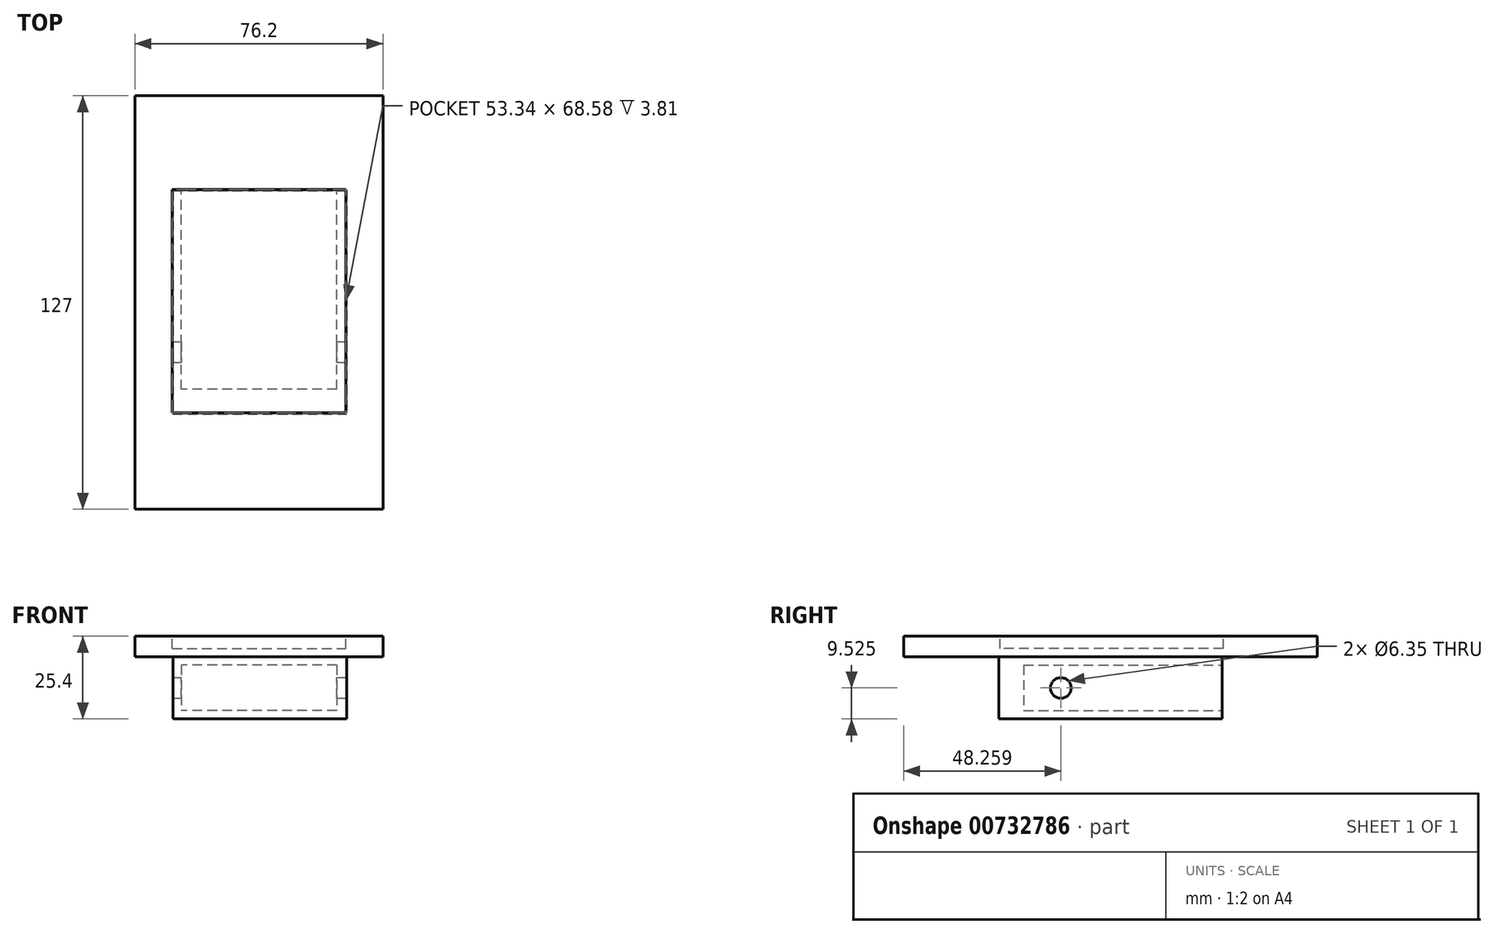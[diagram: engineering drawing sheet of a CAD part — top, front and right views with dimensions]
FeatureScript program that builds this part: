
annotation { "Feature Type Name" : "Feature", "Feature Type Description" : "" }
export const myFeature = defineFeature(function(context is Context, id is Id, definition is map)
    precondition{}
    {
        {
            var Q0;
            Q0=qCreatedBy(makeId("Top.planeOp"),FACE);
            var sketch = newSketch(context, id + "F0", { "sketchPlane" : qUnion([Q0])});
            skLineSegment(sketch, "E0.bottom", {"start": v(-26.47, 33.9) * mm, "end": v(26.87, 33.9) * mm});
            skLineSegment(sketch, "E0.top", {"start": v(-26.47, -34.68) * mm, "end": v(26.87, -34.68) * mm});
            skLineSegment(sketch, "E0.left", {"start": v(-26.47, 33.9) * mm, "end": v(-26.47, -34.68) * mm});
            skLineSegment(sketch, "E0.right", {"start": v(26.87, 33.9) * mm, "end": v(26.87, -34.68) * mm});
            skLineSegment(sketch, "E1.bottom", {"start": v(38.07, 63.1) * mm, "end": v(-38.13, 63.1) * mm});
            skLineSegment(sketch, "E1.top", {"start": v(38.07, -63.9) * mm, "end": v(-38.13, -63.9) * mm});
            skLineSegment(sketch, "E1.left", {"start": v(38.07, 63.1) * mm, "end": v(38.07, -63.9) * mm});
            skLineSegment(sketch, "E1.right", {"start": v(-38.13, 63.1) * mm, "end": v(-38.13, -63.9) * mm});
            skLineSegment(sketch, "E2", {"start": v(-37.68, -0.4) * mm, "end": v(-26.47, -0.4) * mm});
            skLineSegment(sketch, "E3", {"start": v(26.87, -0.4) * mm, "end": v(38.07, -0.4) * mm});
            skLineSegment(sketch, "E4", {"start": v(-0.03, 33.9) * mm, "end": v(-0.03, 63.1) * mm});
            skLineSegment(sketch, "E5", {"start": v(16.32, -63.9) * mm, "end": v(16.32, -34.68) * mm});
            skLineSegment(sketch, "E6", {"start": v(-0.03, 63.1) * mm, "end": v(-0.03, 37.7) * mm});
            skLineSegment(sketch, "E7", {"start": v(-0.03, 37.7) * mm, "end": v(12.67, 37.7) * mm});
            skLineSegment(sketch, "E8.MirrorCS", {"start": v(-0.03, 37.7) * mm, "end": v(-12.73, 37.7) * mm});
            skSolve(sketch);
        }
        {
            var Q0;
            {var subQ4=sQuery(id+"F0.wireOp",EDGE,"E0.left");var subQ10=makeQuery(id+"F0.imprint","IMPRINT",VERTEX,{"derivedFrom":subQ4});Q0=makeQuery(id+"F0.imprint","IMPRINT",FACE,{"disambiguationData":[TD([[makeQuery(id+"F0.imprint","IMPRINT",EDGE,{"disambiguationData":[TD([[subQ10,1.0]])],"derivedFrom":subQ4}),1.0]])]});}
            extrude(context, id + "F1", {"entities" : qUnion([Q0]), "oppositeDirection" : true, "depth" : 19.05 * mm, "offsetDistance" : 25.4 * mm});
        }
        {
            var Q0;
            Q0=makeQuery(id+"F1.opExtrude","SWEPT_FACE",FACE,{"disambiguationData":[OSD([sQuery(id+"F0.wireOp",EDGE,"E0.bottom")])]});
            var sketch = newSketch(context, id + "F2", { "sketchPlane" : qUnion([Q0])});
            skLineSegment(sketch, "E9", {"start": v(26.47, 0) * mm, "end": v(26.47, -19.05) * mm});
            skLineSegment(sketch, "E10", {"start": v(26.47, -19.05) * mm, "end": v(-26.87, -19.05) * mm});
            skLineSegment(sketch, "E11", {"start": v(-26.87, -19.05) * mm, "end": v(-26.87, 0) * mm});
            skLineSegment(sketch, "E12", {"start": v(-26.87, 0) * mm, "end": v(26.47, 0) * mm});
            skLineSegment(sketch, "E13", {"start": v(26.47, 0) * mm, "end": v(23.93, 0) * mm});
            skLineSegment(sketch, "E14", {"start": v(23.93, 0) * mm, "end": v(23.93, -2.54) * mm});
            skLineSegment(sketch, "E15.MirrorCS", {"start": v(-23.93, 0) * mm, "end": v(-23.93, -2.54) * mm});
            skLineSegment(sketch, "E16", {"start": v(-23.93, -2.54) * mm, "end": v(23.93, -2.54) * mm});
            skLineSegment(sketch, "E17", {"start": v(26.47, -19.05) * mm, "end": v(23.93, -19.05) * mm});
            skLineSegment(sketch, "E18", {"start": v(23.93, -19.05) * mm, "end": v(23.93, -16.51) * mm});
            skLineSegment(sketch, "E19.MirrorCS", {"start": v(-23.93, -19.05) * mm, "end": v(-23.93, -16.51) * mm});
            skLineSegment(sketch, "E20", {"start": v(-23.93, -2.54) * mm, "end": v(-23.93, -16.51) * mm});
            skLineSegment(sketch, "E21", {"start": v(-23.93, -16.51) * mm, "end": v(23.93, -16.51) * mm});
            skLineSegment(sketch, "E22", {"start": v(23.93, -2.54) * mm, "end": v(23.93, -16.51) * mm});
            skSolve(sketch);
        }
        {
            var Q0;
            Q0=makeQuery(id+"F2.imprint","IMPRINT",FACE,{"disambiguationData":[TD([[makeQuery(id+"F2.imprint","IMPRINT",EDGE,{"derivedFrom":sQuery(id+"F2.wireOp",EDGE,"E16")}),-1.0]])]});
            extrude(context, id + "F3", {"entities" : qUnion([Q0]), "operationType" : NewBodyOperationType.REMOVE, "oppositeDirection" : true, "depth" : 60.96 * mm, "offsetDistance" : 25.4 * mm});
        }
        {
            var Q0;
            Q0=makeQuery(id+"F0.imprint","IMPRINT",FACE,{"disambiguationData":[TD([[makeQuery(id+"F0.imprint","IMPRINT",EDGE,{"derivedFrom":sQuery(id+"F0.wireOp",EDGE,"gSL48M3m-er1I-eWqx-o3Fm-BarbDNzvo99A.bottom")}),1.0]])]});
            var Q1;
            {var subQ7=sQuery(id+"F0.wireOp",EDGE,"E3");Q1=makeQuery(id+"F0.imprint","IMPRINT",FACE,{"disambiguationData":[TD([[makeQuery(id+"F0.imprint","IMPRINT",EDGE,{"derivedFrom":subQ7}),-1.0]])]});}
            var Q2;
            {var subQ0=sQuery(id+"F0.wireOp",EDGE,"E4");Q2=makeQuery(id+"F0.imprint","IMPRINT",FACE,{"disambiguationData":[TD([[makeQuery(id+"F0.imprint","IMPRINT",EDGE,{"derivedFrom":subQ0}),1.0]])]});}
            var Q3;
            {var subQ0=sQuery(id+"F0.wireOp",EDGE,"b93ae854-abed-4926-95a7-5670e14655770.MirrorCS");Q3=makeQuery(id+"F0.imprint","IMPRINT",FACE,{"disambiguationData":[TD([[makeQuery(id+"F0.imprint","IMPRINT",EDGE,{"derivedFrom":subQ0}),-1.0]])]});}
            var Q4;
            {var subQ3=sQuery(id+"F0.wireOp",EDGE,"E3");Q4=makeQuery(id+"F0.imprint","IMPRINT",FACE,{"disambiguationData":[TD([[makeQuery(id+"F0.imprint","IMPRINT",EDGE,{"derivedFrom":subQ3}),1.0]])]});}
            var Q5;
            {var subQ4=sQuery(id+"F0.wireOp",EDGE,"E0.left");var subQ10=makeQuery(id+"F0.imprint","IMPRINT",VERTEX,{"derivedFrom":subQ4});Q5=makeQuery(id+"F0.imprint","IMPRINT",FACE,{"disambiguationData":[TD([[makeQuery(id+"F0.imprint","IMPRINT",EDGE,{"disambiguationData":[TD([[subQ10,1.0]])],"derivedFrom":subQ4}),1.0]])]});}
            extrude(context, id + "F4", {"entities" : qUnion([Q0, Q1, Q2, Q3, Q4, Q5]), "operationType" : NewBodyOperationType.ADD, "depth" : 6.35 * mm, "offsetDistance" : 25.4 * mm});
        }
        {
            var Q0;
            Q0=makeQuery(id+"F1.opExtrude","SWEPT_FACE",FACE,{"disambiguationData":[OSD([sQuery(id+"F0.wireOp",EDGE,"E0.right")])]});
            var sketch = newSketch(context, id + "F5", { "sketchPlane" : qUnion([Q0])});
            skLineSegment(sketch, "E23", {"start": v(33.9, -19.05) * mm, "end": v(-34.68, -19.05) * mm});
            skLineSegment(sketch, "E24", {"start": v(-34.68, -19.05) * mm, "end": v(-34.68, 0) * mm});
            skLineSegment(sketch, "E25", {"start": v(-34.68, 0) * mm, "end": v(33.9, 0) * mm});
            skLineSegment(sketch, "E26", {"start": v(33.9, 0) * mm, "end": v(33.9, -19.05) * mm});
            skPoint(sketch, "E27", {"position": v(-15.63, -9.52) * mm});
            skPoint(sketch, "E27.positionSnap0", {"position": v(-34.68, -9.52) * mm});
            skSolve(sketch);
        }
        {
            var Q0;
            Q0=sQuery(id+"F5.wireOp",VERTEX,"E27");
            var Q1;
            Q1=makeQuery(id+"F1.opExtrude","SWEPT_BODY",BODY,{"disambiguationData":[OSD([sQuery(id+"F0.wireOp",EDGE,"E0.bottom"),sQuery(id+"F0.wireOp",EDGE,"E0.top"),sQuery(id+"F0.wireOp",EDGE,"E0.left"),sQuery(id+"F0.wireOp",EDGE,"E0.right")])]});
            hole(context, id + "F6", {"style" : HoleStyle.SIMPLE, "endStyle" : HoleEndStyle.THROUGH, "holeDiameter" : 6.35 * mm, "majorDiameter" : 6.35 * mm, "isTappedThrough" : true, "tappedDepth" : 12.7 * mm, "tapClearance" : 3, "locations" : qUnion([Q0]), "scope" : qUnion([Q1])});
        }
        {
            var Q0;
            Q0=makeQuery(id+"F4.opExtrude","CAP_FACE",FACE,{"disambiguationData":[OSD([sQuery(id+"F0.wireOp",EDGE,"E1.bottom"),sQuery(id+"F0.wireOp",EDGE,"E1.top"),sQuery(id+"F0.wireOp",EDGE,"E1.left"),sQuery(id+"F0.wireOp",EDGE,"E1.right")])],"isStart":false});
            var sketch = newSketch(context, id + "F7", { "sketchPlane" : qUnion([Q0])});
            skLineSegment(sketch, "E28", {"start": v(0, 0) * mm, "end": v(26.67, 0) * mm});
            skLineSegment(sketch, "E29", {"start": v(26.67, 0) * mm, "end": v(26.67, 34.3) * mm});
            skLineSegment(sketch, "E30.MirrorCS", {"start": v(-26.67, 0) * mm, "end": v(-26.67, 34.3) * mm});
            skLineSegment(sketch, "E31.MirrorCS", {"start": v(26.67, 0) * mm, "end": v(26.67, -34.3) * mm});
            skLineSegment(sketch, "E32.MirrorCS", {"start": v(-26.67, 0) * mm, "end": v(-26.67, -34.3) * mm});
            skLineSegment(sketch, "E33", {"start": v(-26.67, 34.3) * mm, "end": v(26.67, 34.3) * mm});
            skLineSegment(sketch, "E34", {"start": v(26.67, -34.3) * mm, "end": v(-26.67, -34.3) * mm});
            skSolve(sketch);
        }
        {
            var Q0;
            Q0=makeQuery(id+"F7.imprint","IMPRINT",FACE,{"disambiguationData":[TD([[makeQuery(id+"F7.imprint","IMPRINT",EDGE,{"derivedFrom":sQuery(id+"F7.wireOp",EDGE,"E29")}),1.0]])]});
            extrude(context, id + "F8", {"entities" : qUnion([Q0]), "operationType" : NewBodyOperationType.REMOVE, "oppositeDirection" : true, "depth" : 3.8 * mm, "offsetDistance" : 25.4 * mm});
        }
    });
